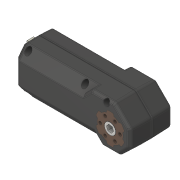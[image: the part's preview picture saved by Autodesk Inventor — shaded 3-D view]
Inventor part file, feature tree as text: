
AUTODESK INVENTOR PART (.ipt)
format: ipt  version: 2018 (Build 220112000, 112)  size: 7,502,848 bytes
history: native  units: in
note: dims shown in document units (in); Inventor stores cm internally (conversion verified against a paired STEP export)
features: other x10, plane x2
ambient origin geometry x8: Origin, YZ Plane, XZ Plane, XY Plane, X Axis, Y Axis, Z Axis, Center Point
bodies: Solid1 (feature_tree), Solid2 (feature_tree), Solid3 (feature_tree), Solid4 (feature_tree), Solid5 (feature_tree), Solid6 (feature_tree), Solid7 (feature_tree), Solid8 (feature_tree)
feature tree (12):
  plane  "Work Plane1"
  plane  "Work Plane2"
  parser-record x1  (decoder bookkeeping rows leaked as tree rows — omitted from the tree; the rows remain in map.json)
  other  "NONE:1"
  other  "NONE:2"
  other  "NONE:3"
  other  "NONE:4"
  other  "NONE:5"
  other  "NONE:6"
  other  "NONE:7"
  other  "Composite1"
  other  "Srf1"
